# Revit family: QF_Brema_CB246A_CB246W_cat
name_source: partatom
category: Specialty Equipment
revit_build: Autodesk Revit MEP 2012 (Build: 20110916_2132(x64)
units: mm (PartAtom-declared; Revit-internal decimal feet)

## types (2) — shared parameters
Apparent Power = 350 VA
Assembly Code = E1090320
BTUH = 0 W
Cold Water Connection Height = 175 mm  [stored 0.574147 ft]
Cold Water Maximum Pressure = 6.0 bar
Cold Water Minimum Pressure = 1.0 bar
Cold Water Size = 1"
Cold Water Size Radius = 1/2"
Conn Conduit = Yes
Cycle = 50 Hz
Depth = 460 mm  [stored 1.50919 ft]
Elec Conn Connection Height = 211 mm  [stored 0.692257 ft]
FL Amps = 0 A
Height = 610 mm  [stored 2.00131 ft]
Indirect Waste Connection Height = 130 mm  [stored 0.426509 ft]
Indirect Waste Radius = 1/2"
Indirect Waste Size = 1"
Manufacturer = BREMA
Max Overcurrent Protection = 10 A
Min Ckt Ampacity = 0 A
Phase = 1
Refrigerant Type = R404A
URL = www.bremaice.it
Volts = 230 V
Watts = 350 W
Width = 390 mm  [stored 1.27953 ft]

## per-type parameters (varying)
| type | Description | Weight |
| CB246A | AUTOMATIC ICE CUBE MAKER AIR COOLED | 35 kg |
| CB246W | AUTOMATIC ICE CUBE MAKER WATER COOLED | 41 kg |

note: column(s) folded — value = type name in every type: Model

note: [stored X ft] marks values corroborated as IEEE doubles in the binary element streams (Revit-internal decimal feet)

## geometry (parser evidence)
native form markers: Blend x7, Sweep x2
no freeform markers — native parametric forms only
